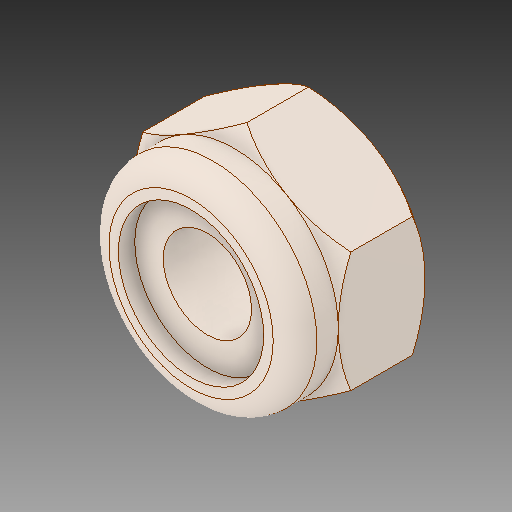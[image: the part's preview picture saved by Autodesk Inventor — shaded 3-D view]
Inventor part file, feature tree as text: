
AUTODESK INVENTOR PART (.ipt)
format: ipt  version: 2018 (Build 220112000, 112)  size: 166,912 bytes
history: native  units: in
note: dims shown in document units (in); Inventor stores cm internally (conversion verified against a paired STEP export)
features: fillet x1
ambient origin geometry x8: Origin, YZ Plane, XZ Plane, XY Plane, X Axis, Y Axis, Z Axis, Center Point
bodies: Solid1 (feature_tree)
feature tree (1):
  fillet  "Fillet1"  [1 undecoded]
note: 1 required parameter value undecoded (feature->parameter linkage not recoverable at this tier; creation-order binding heuristic only, values carry confidence <= 0.55)
